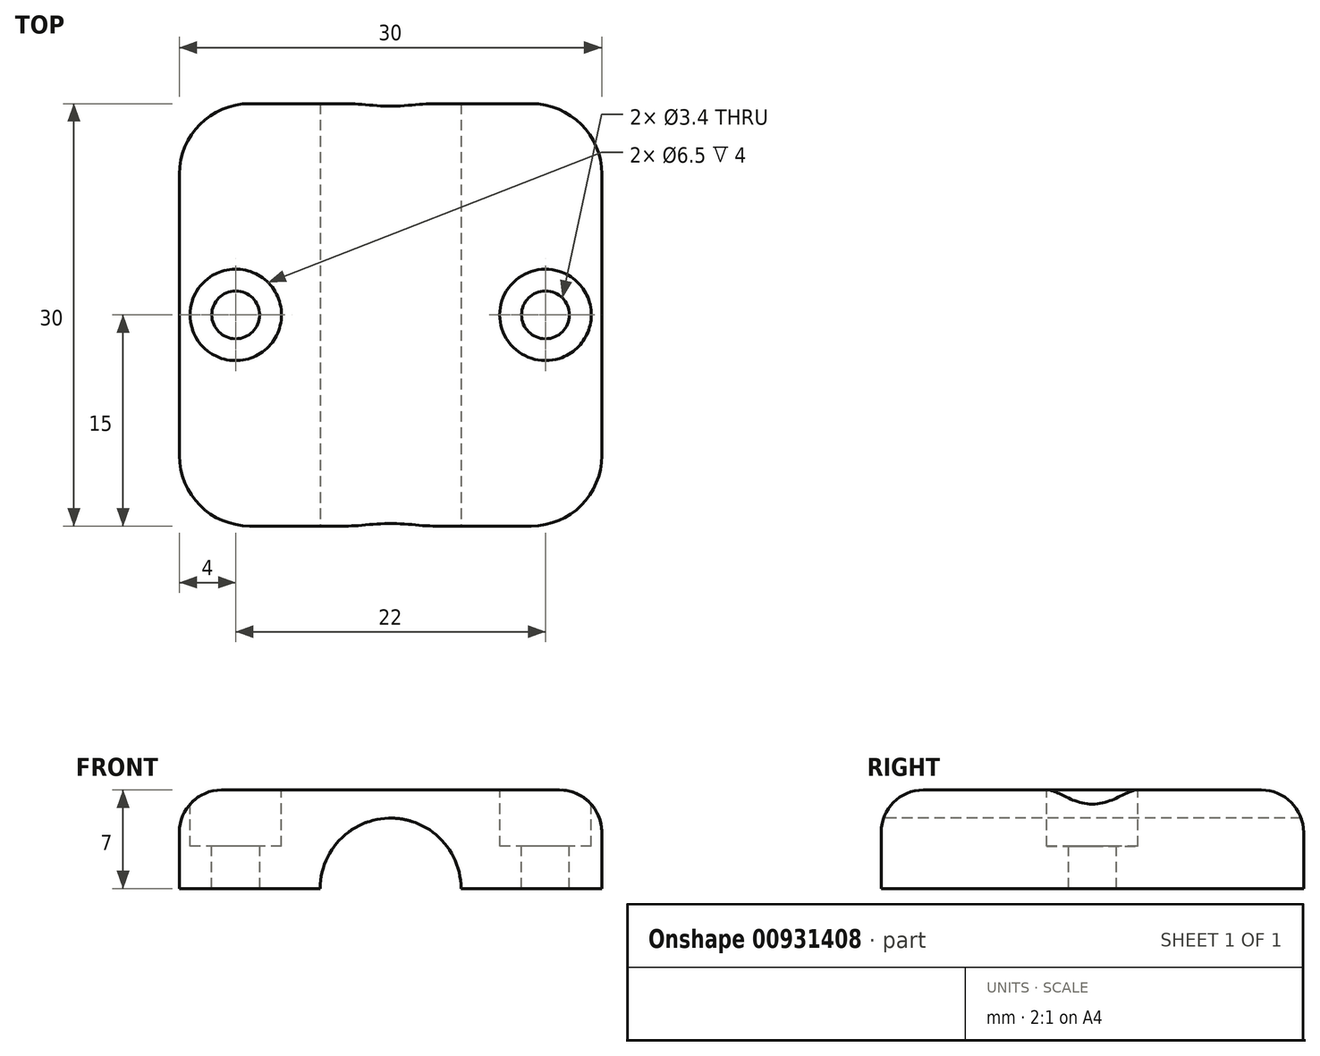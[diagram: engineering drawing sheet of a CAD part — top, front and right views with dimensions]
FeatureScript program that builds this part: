
annotation { "Feature Type Name" : "Feature", "Feature Type Description" : "" }
export const myFeature = defineFeature(function(context is Context, id is Id, definition is map)
    precondition{}
    {
        {
            var Q0;
            Q0=qCreatedBy(makeId("Top.planeOp"),FACE);
            var sketch = newSketch(context, id + "F0", { "sketchPlane" : qUnion([Q0])});
            skLineSegment(sketch, "E0.bottom", {"start": v(15, -15) * mm, "end": v(-15, -15) * mm});
            skLineSegment(sketch, "E0.top", {"start": v(15, 15) * mm, "end": v(-15, 15) * mm});
            skLineSegment(sketch, "E0.left", {"start": v(15, -15) * mm, "end": v(15, 15) * mm});
            skLineSegment(sketch, "E0.right", {"start": v(-15, -15) * mm, "end": v(-15, 15) * mm});
            skPoint(sketch, "E0.middle", {"position": v(0, 0) * mm});
            skSolve(sketch);
        }
        {
            var Q0;
            Q0=makeQuery(id+"F0.imprint","IMPRINT",FACE,{"disambiguationData":[TD([[makeQuery(id+"F0.imprint","IMPRINT",EDGE,{"derivedFrom":sQuery(id+"F0.wireOp",EDGE,"E0.bottom")}),-1.0]])]});
            extrude(context, id + "F1", {"entities" : qUnion([Q0]), "depth" : 7 * mm, "offsetDistance" : 25 * mm});
        }
        {
            var Q0;
            Q0=makeQuery(id+"F1.opExtrude","CAP_FACE",FACE,{"disambiguationData":[OSD([sQuery(id+"F0.wireOp",EDGE,"E0.bottom"),sQuery(id+"F0.wireOp",EDGE,"E0.top"),sQuery(id+"F0.wireOp",EDGE,"E0.left"),sQuery(id+"F0.wireOp",EDGE,"E0.right")])],"isStart":false});
            var sketch = newSketch(context, id + "F2", { "sketchPlane" : qUnion([Q0])});
            skPoint(sketch, "E1", {"position": v(-11, 0) * mm});
            skPoint(sketch, "E2", {"position": v(11, 0) * mm});
            skSolve(sketch);
        }
        {
            var Q0;
            Q0=sQuery(id+"F2.wireOp",VERTEX,"E1");
            var Q1;
            Q1=sQuery(id+"F2.wireOp",VERTEX,"E2");
            var Q2;
            Q2=makeQuery(id+"F1.opExtrude","SWEPT_BODY",BODY,{"disambiguationData":[OSD([sQuery(id+"F0.wireOp",EDGE,"E0.bottom"),sQuery(id+"F0.wireOp",EDGE,"E0.top"),sQuery(id+"F0.wireOp",EDGE,"E0.left"),sQuery(id+"F0.wireOp",EDGE,"E0.right")])]});
            hole(context, id + "F3", {"style" : HoleStyle.C_BORE, "endStyle" : HoleEndStyle.THROUGH, "holeDiameter" : 3.4 * mm, "cBoreDiameter" : 6.5 * mm, "cBoreDepth" : 4 * mm, "majorDiameter" : 5 * mm, "isTappedThrough" : true, "tappedDepth" : 12 * mm, "tapClearance" : 3, "locations" : qUnion([Q0, Q1]), "scope" : qUnion([Q2])});
        }
        {
            var Q0;
            Q0=makeQuery(id+"F1.opExtrude","SWEPT_FACE",FACE,{"disambiguationData":[OSD([sQuery(id+"F0.wireOp",EDGE,"E0.bottom")])]});
            var sketch = newSketch(context, id + "F4", { "sketchPlane" : qUnion([Q0])});
            skCircle(sketch, "E3", {"center": v(0, 0) * mm, "radius": 5 * mm});
            skSolve(sketch);
        }
        {
            var Q0;
            {var subQ0=sQuery(id+"F4.wireOp",EDGE,"E3");var subQ1=makeQuery(id+"F1.opExtrude","CAP_EDGE",EDGE,{"disambiguationData":[OSD([sQuery(id+"F0.wireOp",EDGE,"E0.bottom")])],"isStart":true});var subQ2=makeQuery(id+"F4.imprint","INTERSECT",VERTEX,{"disambiguationData":[OD(0.0)],"derivedFrom":[subQ1,subQ0]});Q0=makeQuery(id+"F4.imprint","IMPRINT",FACE,{"disambiguationData":[TD([[makeQuery(id+"F4.imprint","IMPRINT",EDGE,{"disambiguationData":[TD([[subQ2,-1.0]])],"derivedFrom":subQ0}),1.0]])]});}
            extrude(context, id + "F5", {"entities" : qUnion([Q0]), "operationType" : NewBodyOperationType.REMOVE, "endBound" : BoundingType.UP_TO_NEXT, "oppositeDirection" : true, "depth" : 25 * mm, "offsetDistance" : 25 * mm});
        }
        {
            var Q0;
            Q0=makeQuery(id+"F1.opExtrude","SWEPT_EDGE",EDGE,{"disambiguationData":[OSD([sQuery(id+"F0.wireOp",EDGE,"E0.bottom"),sQuery(id+"F0.wireOp",EDGE,"E0.left")])]});
            var Q1;
            Q1=makeQuery(id+"F1.opExtrude","SWEPT_EDGE",EDGE,{"disambiguationData":[OSD([sQuery(id+"F0.wireOp",EDGE,"E0.bottom"),sQuery(id+"F0.wireOp",EDGE,"E0.right")])]});
            var Q2;
            Q2=makeQuery(id+"F1.opExtrude","SWEPT_EDGE",EDGE,{"disambiguationData":[OSD([sQuery(id+"F0.wireOp",EDGE,"E0.top"),sQuery(id+"F0.wireOp",EDGE,"E0.left")])]});
            var Q3;
            Q3=makeQuery(id+"F1.opExtrude","SWEPT_EDGE",EDGE,{"disambiguationData":[OSD([sQuery(id+"F0.wireOp",EDGE,"E0.top"),sQuery(id+"F0.wireOp",EDGE,"E0.right")])]});
            fillet(context, id + "F6", {"entities" : qUnion([Q0, Q1, Q2, Q3]), "radius" : 5 * mm, "tangentPropagation" : true, "allowEdgeOverflow" : false});
        }
        {
            var Q0;
            {var subQ0=sQuery(id+"F0.wireOp",EDGE,"E0.right");var subQ1=sQuery(id+"F0.wireOp",EDGE,"E0.bottom");Q0=makeQuery(id+"F6.opFillet","BLEND_EDGE",EDGE,{"blendedFrom":[makeQuery(id+"F1.opExtrude","SWEPT_EDGE",EDGE,{"disambiguationData":[OSD([subQ1,subQ0])]}),makeQuery(id+"F1.opExtrude","CAP_FACE",FACE,{"disambiguationData":[OSD([subQ1,sQuery(id+"F0.wireOp",EDGE,"E0.top"),sQuery(id+"F0.wireOp",EDGE,"E0.left"),subQ0])],"isStart":false})],"blendedInto":[makeQuery(id+"F1.opExtrude","CAP_FACE",FACE,{"disambiguationData":[OSD([subQ1,sQuery(id+"F0.wireOp",EDGE,"E0.top"),sQuery(id+"F0.wireOp",EDGE,"E0.left"),subQ0])],"isStart":false})]});}
            fillet(context, id + "F7", {"entities" : qUnion([Q0]), "radius" : 3 * mm, "tangentPropagation" : true, "allowEdgeOverflow" : false});
        }
    });
